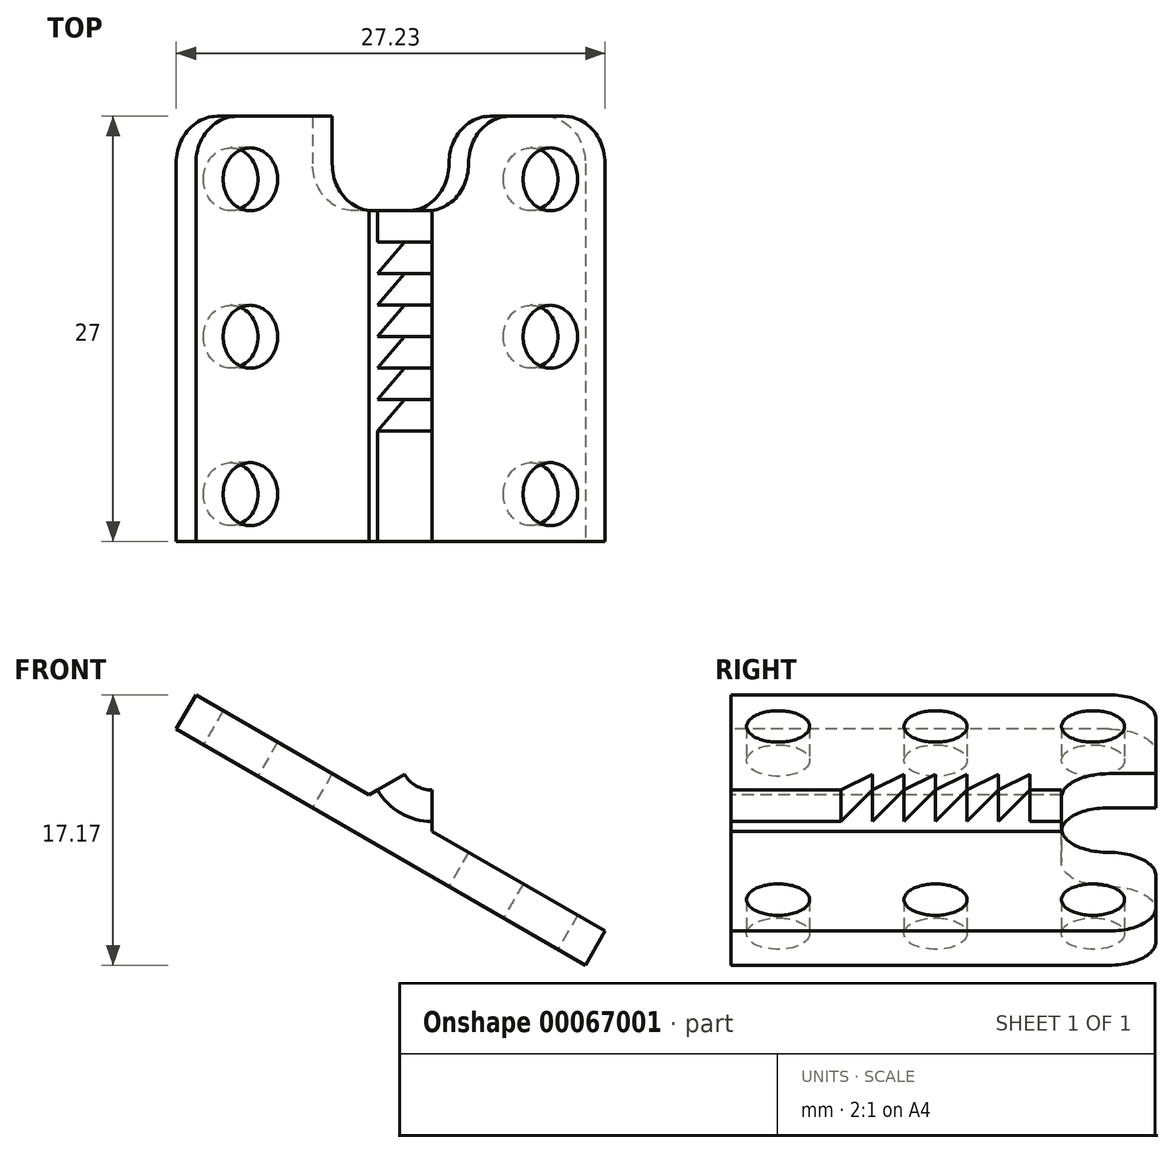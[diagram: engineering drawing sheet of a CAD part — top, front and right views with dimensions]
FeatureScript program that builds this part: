
annotation { "Feature Type Name" : "Feature", "Feature Type Description" : "" }
export const myFeature = defineFeature(function(context is Context, id is Id, definition is map)
    precondition{}
    {
        {
            var Q0;
            Q0=qCreatedBy(makeId("Right.planeOp"),FACE);
            var sketch = newSketch(context, id + "F0", { "sketchPlane" : qUnion([Q0])});
            skLineSegment(sketch, "E0", {"start": v(-1, 0) * mm, "end": v(7, 0) * mm});
            skLineSegment(sketch, "E1", {"start": v(7, 0) * mm, "end": v(9, 2) * mm});
            skLineSegment(sketch, "E2", {"start": v(9, 2) * mm, "end": v(9, 0) * mm});
            skLineSegment(sketch, "E3", {"start": v(9, 0) * mm, "end": v(11, 2) * mm});
            skLineSegment(sketch, "E4", {"start": v(11, 2) * mm, "end": v(11, 0) * mm});
            skLineSegment(sketch, "E5", {"start": v(11, 0) * mm, "end": v(13, 2) * mm});
            skLineSegment(sketch, "E6", {"start": v(13, 2) * mm, "end": v(13, 0) * mm});
            skLineSegment(sketch, "E7", {"start": v(13, 0) * mm, "end": v(15, 2) * mm});
            skLineSegment(sketch, "E8", {"start": v(15, 2) * mm, "end": v(15, 0) * mm});
            skLineSegment(sketch, "E9", {"start": v(15, 0) * mm, "end": v(17, 2) * mm});
            skLineSegment(sketch, "E10", {"start": v(17, 2) * mm, "end": v(17, 0) * mm});
            skLineSegment(sketch, "E11", {"start": v(17, 0) * mm, "end": v(19, 2) * mm});
            skLineSegment(sketch, "E12", {"start": v(19, 2) * mm, "end": v(19, 0) * mm});
            skLineSegment(sketch, "E13", {"start": v(19, 0) * mm, "end": v(26, 0) * mm});
            skLineSegment(sketch, "E14", {"start": v(26, 0) * mm, "end": v(26, -2.5) * mm});
            skLineSegment(sketch, "E15", {"start": v(26, -2.5) * mm, "end": v(0, -2.5) * mm});
            skLineSegment(sketch, "E16", {"start": v(0, -2.5) * mm, "end": v(0, 0) * mm});
            skLineSegment(sketch, "E17", {"start": v(-2.86, 4) * mm, "end": v(29.47, 4) * mm, "construction": true});
            skSolve(sketch);
        }
        {
            var Q0;
            Q0 = qSketchRegion(id + "F0", true);
            var Q1;
            Q1=sQuery(id+"F0.wireOp",EDGE,"E17");
            revolve(context, id + "F1", {"entities" : qUnion([Q0]), "axis" : qUnion([Q1]), "revolveType" : RevolveType.ONE_DIRECTION, "angle" : 60 * degree});
        }
        {
            var Q0;
            Q0=makeQuery(id+"F1.opRevolve","SWEPT_FACE",FACE,{"disambiguationData":[OSD([sQuery(id+"F0.wireOp",EDGE,"E16")])]});
            var sketch = newSketch(context, id + "F2", { "sketchPlane" : qUnion([Q0])});
            skLineSegment(sketch, "E18", {"start": v(0, 4) * mm, "end": v(-5.44, -5.43) * mm, "construction": true});
            skLineSegment(sketch, "E19", {"start": v(-2, 0.54) * mm, "end": v(-3.25, -1.63) * mm});
            skLineSegment(sketch, "E20", {"start": v(-3.25, -1.63) * mm, "end": v(9.74, -9.13) * mm});
            skLineSegment(sketch, "E21", {"start": v(9.74, -9.13) * mm, "end": v(11, -6.96) * mm});
            skLineSegment(sketch, "E22", {"start": v(11, -6.96) * mm, "end": v(-2, 0.54) * mm});
            skLineSegment(sketch, "E23", {"start": v(-2, 0.54) * mm, "end": v(-15, 8.04) * mm});
            skLineSegment(sketch, "E24", {"start": v(-15, 8.04) * mm, "end": v(-16.24, 5.87) * mm});
            skLineSegment(sketch, "E25", {"start": v(-16.24, 5.87) * mm, "end": v(-3.25, -1.63) * mm});
            skSolve(sketch);
        }
        {
            var Q0;
            Q0 = qSketchRegion(id + "F2", true);
            extrude(context, id + "F3", {"entities" : qUnion([Q0]), "operationType" : NewBodyOperationType.ADD, "oppositeDirection" : true, "depth" : 27 * mm});
        }
        {
            var Q0;
            Q0=makeQuery(id+"F3.opExtrude","SWEPT_FACE",FACE,{"disambiguationData":[OSD([sQuery(id+"F2.wireOp",EDGE,"E20"),sQuery(id+"F2.wireOp",EDGE,"E25")])]});
            var sketch = newSketch(context, id + "F4", { "sketchPlane" : qUnion([Q0])});
            skCircle(sketch, "E26", {"center": v(-13, -3) * mm, "radius": 2 * mm});
            skCircle(sketch, "E27.1.0.0", {"center": v(9, -3) * mm, "radius": 2 * mm});
            skLineSegment(sketch, "E27.direction1", {"start": v(9, -3) * mm, "end": v(-13, -3) * mm, "construction": true});
            skCircle(sketch, "E28", {"center": v(-13, -13) * mm, "radius": 2 * mm});
            skCircle(sketch, "E29", {"center": v(9, -13) * mm, "radius": 2 * mm});
            skCircle(sketch, "E30", {"center": v(-13, -23) * mm, "radius": 2 * mm});
            skCircle(sketch, "E31", {"center": v(9, -23) * mm, "radius": 2 * mm});
            skSolve(sketch);
        }
        {
            var Q0;
            Q0 = qSketchRegion(id + "F4", true);
            extrude(context, id + "F5", {"entities" : qUnion([Q0]), "operationType" : NewBodyOperationType.REMOVE, "endBound" : BoundingType.THROUGH_ALL, "oppositeDirection" : true, "depth" : 25 * mm});
        }
        {
            var Q0;
            Q0=makeQuery(id+"F3.opExtrude","SWEPT_FACE",FACE,{"disambiguationData":[OSD([sQuery(id+"F2.wireOp",EDGE,"E20"),sQuery(id+"F2.wireOp",EDGE,"E25")])]});
            var sketch = newSketch(context, id + "F6", { "sketchPlane" : qUnion([Q0])});
            skLineSegment(sketch, "E32.bottom", {"start": v(3, -27) * mm, "end": v(-7, -27) * mm});
            skLineSegment(sketch, "E32.top", {"start": v(3, -21) * mm, "end": v(-7, -21) * mm});
            skLineSegment(sketch, "E32.left", {"start": v(3, -27) * mm, "end": v(3, -21) * mm});
            skLineSegment(sketch, "E32.right", {"start": v(-7, -27) * mm, "end": v(-7, -21) * mm});
            skSolve(sketch);
        }
        {
            var Q0;
            Q0 = qSketchRegion(id + "F6", true);
            extrude(context, id + "F7", {"entities" : qUnion([Q0]), "operationType" : NewBodyOperationType.REMOVE, "endBound" : BoundingType.THROUGH_ALL, "oppositeDirection" : true, "depth" : 25 * mm});
        }
        {
            var Q0;
            Q0=makeQuery(id+"F7.boolean.opBoolean","COPY",EDGE,{"derivedFrom":makeQuery(id+"F7.opExtrude","SWEPT_EDGE",EDGE,{"disambiguationData":[OSD([sQuery(id+"F6.wireOp",EDGE,"E32.top"),sQuery(id+"F6.wireOp",EDGE,"E32.left")])]})});
            var Q1;
            Q1=makeQuery(id+"F7.boolean.opBoolean","COPY",EDGE,{"derivedFrom":makeQuery(id+"F7.opExtrude","SWEPT_EDGE",EDGE,{"disambiguationData":[OSD([sQuery(id+"F2.wireOp",EDGE,"E20"),sQuery(id+"F2.wireOp",EDGE,"E25"),sQuery(id+"F6.wireOp",EDGE,"E32.bottom"),sQuery(id+"F6.wireOp",EDGE,"E32.left")])]})});
            var Q2;
            Q2=makeQuery(id+"F7.boolean.opBoolean","COPY",EDGE,{"derivedFrom":makeQuery(id+"F7.opExtrude","SWEPT_EDGE",EDGE,{"disambiguationData":[OSD([sQuery(id+"F2.wireOp",EDGE,"E20"),sQuery(id+"F2.wireOp",EDGE,"E25"),sQuery(id+"F6.wireOp",EDGE,"E32.bottom"),sQuery(id+"F6.wireOp",EDGE,"E32.right")])]})});
            var Q3;
            Q3=makeQuery(id+"F7.boolean.opBoolean","COPY",EDGE,{"derivedFrom":makeQuery(id+"F7.opExtrude","SWEPT_EDGE",EDGE,{"disambiguationData":[OSD([sQuery(id+"F6.wireOp",EDGE,"E32.top"),sQuery(id+"F6.wireOp",EDGE,"E32.right")])]})});
            var Q4;
            Q4=makeQuery(id+"F3.opExtrude","CAP_EDGE",EDGE,{"disambiguationData":[OSD([sQuery(id+"F2.wireOp",EDGE,"E24")])],"isStart":false});
            var Q5;
            Q5=makeQuery(id+"F3.opExtrude","CAP_EDGE",EDGE,{"disambiguationData":[OSD([sQuery(id+"F2.wireOp",EDGE,"E21")])],"isStart":false});
            fillet(context, id + "F8", {"entities" : qUnion([Q0, Q1, Q2, Q3, Q4, Q5]), "radius" : 3 * mm, "tangentPropagation" : true, "allowEdgeOverflow" : false});
        }
    });
